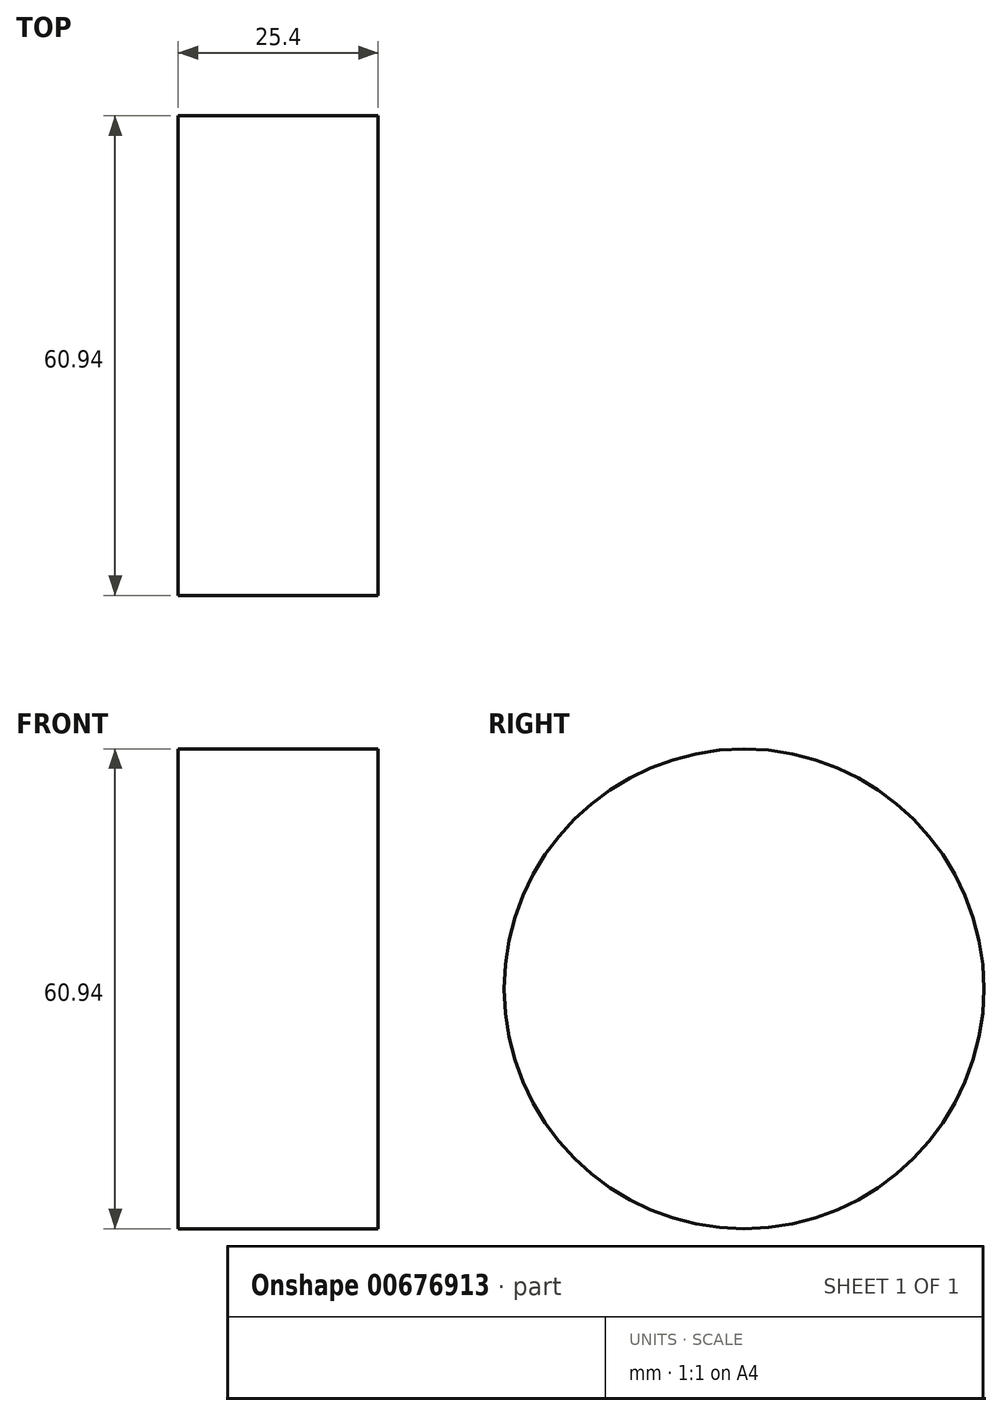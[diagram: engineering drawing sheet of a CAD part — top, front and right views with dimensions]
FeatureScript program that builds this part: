
annotation { "Feature Type Name" : "Feature", "Feature Type Description" : "" }
export const myFeature = defineFeature(function(context is Context, id is Id, definition is map)
    precondition{}
    {
        {
            var Q0;
            Q0=qCreatedBy(makeId("Right.planeOp"),FACE);
            var sketch = newSketch(context, id + "F0", { "sketchPlane" : qUnion([Q0])});
            skCircle(sketch, "E0", {"center": v(0, 0) * mm, "radius": 30.47 * mm});
            skSolve(sketch);
        }
        {
            var Q0;
            Q0=makeQuery(id+"F0.imprint","IMPRINT",FACE,{"disambiguationData":[TD([[makeQuery(id+"F0.imprint","IMPRINT",EDGE,{"derivedFrom":sQuery(id+"F0.wireOp",EDGE,"E0")}),1.0]])]});
            extrude(context, id + "F1", {"entities" : qUnion([Q0]), "depth" : 12.7 * mm, "offsetDistance" : 25.4 * mm, "hasSecondDirection" : true, "secondDirectionOppositeDirection" : true, "secondDirectionDepth" : 12.7 * mm});
        }
    });
